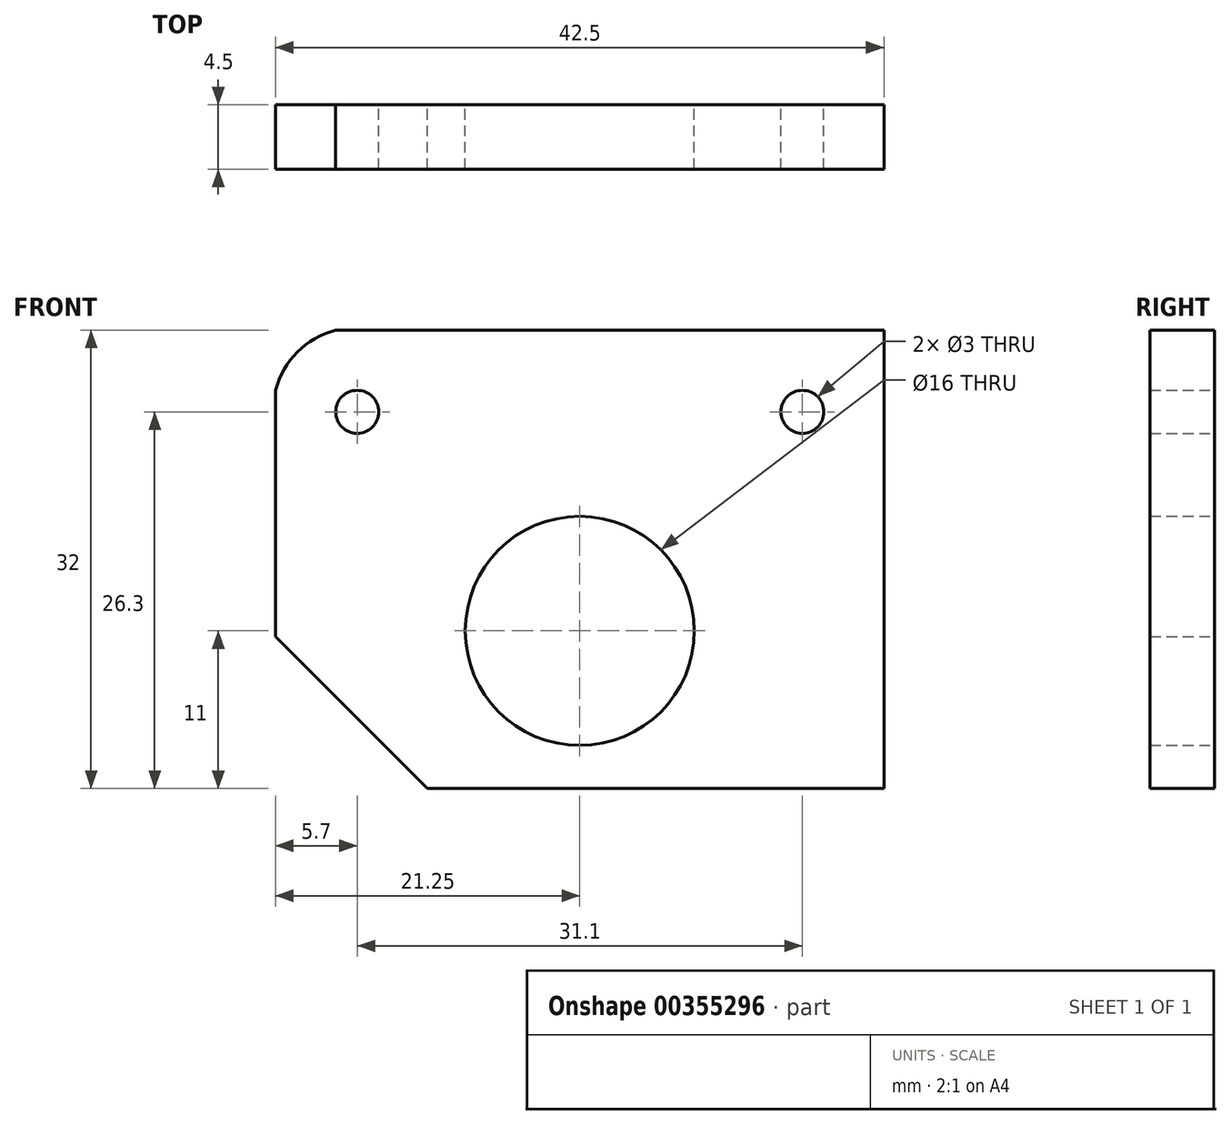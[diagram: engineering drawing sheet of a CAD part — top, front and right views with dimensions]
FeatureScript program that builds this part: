
annotation { "Feature Type Name" : "Feature", "Feature Type Description" : "" }
export const myFeature = defineFeature(function(context is Context, id is Id, definition is map)
    precondition{}
    {
        {
            var Q0;
            Q0=qCreatedBy(makeId("Front.planeOp"),FACE);
            var sketch = newSketch(context, id + "F0", { "sketchPlane" : qUnion([Q0])});
            skLineSegment(sketch, "E0.bottom", {"start": v(21.25, -16) * mm, "end": v(-21.25, -16) * mm});
            skLineSegment(sketch, "E0.top", {"start": v(21.25, 16) * mm, "end": v(-21.25, 16) * mm});
            skLineSegment(sketch, "E0.left", {"start": v(21.25, -16) * mm, "end": v(21.25, 16) * mm});
            skLineSegment(sketch, "E0.right", {"start": v(-21.25, -16) * mm, "end": v(-21.25, 16) * mm});
            skPoint(sketch, "E0.middle", {"position": v(0, 0) * mm});
            skLineSegment(sketch, "E1", {"start": v(0, 16) * mm, "end": v(0, -26) * mm, "construction": true});
            skPoint(sketch, "E1.endSnap0", {"position": v(0, -16) * mm});
            skCircle(sketch, "E2", {"center": v(0, -5) * mm, "radius": 6 * mm});
            skCircle(sketch, "E3", {"center": v(-15.55, 10.3) * mm, "radius": 1.5 * mm});
            skCircle(sketch, "E4", {"center": v(15.55, 10.3) * mm, "radius": 1.5 * mm});
            skLineSegment(sketch, "E5", {"start": v(-21.25, -5.4) * mm, "end": v(-10.64, -16) * mm});
            skCircle(sketch, "E6.0", {"center": v(0, -5) * mm, "radius": 8 * mm});
            skCircle(sketch, "E7", {"center": v(-15.55, 10.3) * mm, "radius": 5.9 * mm});
            skArc(sketch, "E8", {"start": v(4.8, -16) * mm, "mid": v(0, 7) * mm, "end": v(-4.8, -16) * mm});
            skArc(sketch, "E9.0", {"start": v(11.62, -16) * mm, "mid": v(11.41, 6.21) * mm, "end": v(-10.79, 6.81) * mm});
            skArc(sketch, "E10.trimOffspring", {"start": v(-11.99, 5.6) * mm, "mid": v(-16, -5.27) * mm, "end": v(-11.62, -16) * mm});
            skSolve(sketch);
        }
        {
            var Q0;
            {var subQ0=sQuery(id+"F0.wireOp",EDGE,"E0.left");Q0=makeQuery(id+"F0.imprint","IMPRINT",FACE,{"disambiguationData":[TD([[makeQuery(id+"F0.imprint","IMPRINT",EDGE,{"derivedFrom":subQ0}),1.0]])]});}
            var Q1;
            {var subQ0=sQuery(id+"F0.wireOp",EDGE,"E5");var subQ1=sQuery(id+"F0.wireOp",EDGE,"E0.right");var subQ2=makeQuery(id+"F0.imprint","INTERSECT",VERTEX,{"derivedFrom":[subQ1,subQ0]});Q1=makeQuery(id+"F0.imprint","IMPRINT",FACE,{"disambiguationData":[TD([[makeQuery(id+"F0.imprint","IMPRINT",EDGE,{"disambiguationData":[TD([[subQ2,-1.0]])],"derivedFrom":subQ1}),-1.0]])]});}
            var Q2;
            Q2=makeQuery(id+"F0.imprint","IMPRINT",FACE,{"disambiguationData":[TD([[makeQuery(id+"F0.imprint","IMPRINT",EDGE,{"derivedFrom":sQuery(id+"F0.wireOp",EDGE,"E3")}),-1.0]])]});
            var Q3;
            {var subQ8=sQuery(id+"F0.wireOp",EDGE,"E8");Q3=makeQuery(id+"F0.imprint","IMPRINT",FACE,{"disambiguationData":[TD([[makeQuery(id+"F0.imprint","IMPRINT",EDGE,{"derivedFrom":subQ8}),-1.0]])]});}
            var Q4;
            Q4=makeQuery(id+"F0.imprint","IMPRINT",FACE,{"disambiguationData":[TD([[makeQuery(id+"F0.imprint","IMPRINT",EDGE,{"derivedFrom":sQuery(id+"F0.wireOp",EDGE,"E6.0")}),-1.0]])]});
            extrude(context, id + "F1", {"entities" : qUnion([Q0, Q1, Q2, Q3, Q4]), "depth" : 4.5 * mm});
        }
    });
